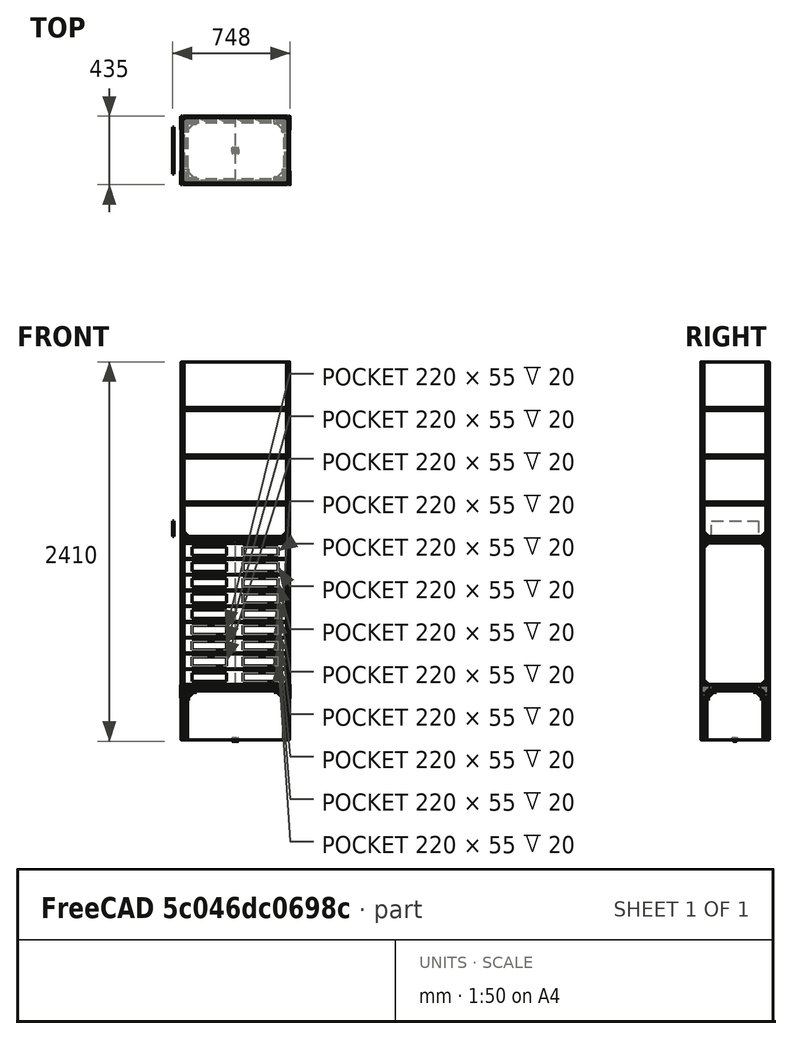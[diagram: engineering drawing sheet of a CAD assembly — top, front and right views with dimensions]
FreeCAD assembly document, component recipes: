
FREECAD ASSEMBLY — COMPONENT RECIPES ("2020 shelf")

This assembly document has 11 components, labeled P0..P10 below (a component is one placed body or linked part). 9 of them carry a construction recipe — the FreeCAD feature program that regenerates the part from scratch, quoted from this document or its linked companion documents; the rest are supplied as boundary geometry only. No exploded tour is included for this assembly.
COMPONENT P0 — recipe-attached ("Cabinet", modeled in this document).
Construction recipe (the document's own serialized feature program — sketch geometry with constraints, then the solid features built on it; lengths are millimeters unless a unit is written):

FEATURE [Sketcher::SketchObject] Sketch016
  ArcFitTolerance = 1e-06
  AttachmentSupport = -> [XY_Plane007]
  FullyConstrained = true
  MakeInternals = false
  MapMode = 5
  sketch-geometry (8):
    g0: LineSegment StartX=20 StartY=0 StartZ=0 EndX=305 EndY=0 EndZ=0
    g1: LineSegment StartX=325 StartY=20 StartZ=0 EndX=325 EndY=435 EndZ=0
    g2: LineSegment StartX=325 StartY=435 StartZ=0 EndX=0 EndY=435 EndZ=0
    g3: LineSegment StartX=0 StartY=435 StartZ=0 EndX=0 EndY=20 EndZ=0
    g4: ArcOfCircle CenterX=20 CenterY=20 CenterZ=0 NormalX=0 NormalY=0 NormalZ=1 AngleXU=0 Radius=20 StartAngle=3.14159 EndAngle=4.71239
    g5: GeomPoint [constr] X=0 Y=0 Z=0
    g6: ArcOfCircle CenterX=305 CenterY=20 CenterZ=0 NormalX=0 NormalY=0 NormalZ=1 AngleXU=0 Radius=20 StartAngle=4.71239 EndAngle=6.28319
    g7: GeomPoint [constr] X=325 Y=0 Z=0
  constraints (19):
    c: Coincident(g1,g2)
    c: Coincident(g2,g3)
    c: Horizontal(g0)
    c: Horizontal(g2)
    c: Vertical(g1)
    c: Vertical(g3)
    c: Coincident(g5,g-1)
    c: DistanceX(g5,g7) = 325
    c: DistanceY(g7,g1) = 435
    c: PointOnObject(g5,g3)
    c: PointOnObject(g5,g0)
    c: Tangent(g3,g4) = -1.5708
    c: Tangent(g0,g4) = -1.5708
    c: PointOnObject(g7,g0)
    c: PointOnObject(g7,g1)
    c: Tangent(g0,g6) = -1.5708
    c: Tangent(g1,g6) = -1.5708
    c: Equal(g4,g6)
    c: Radius(g6) = 20
FEATURE [PartDesign::Pad] Pad009
  Direction = (0,0,1)
  Length = 920
  Length2 = 10
  Profile = -> Sketch016
  ReferenceAxis = -> Sketch016 [N_Axis]
  Suppressed = false
  Type = 0
FEATURE [Sketcher::SketchObject] Sketch017
  ArcFitTolerance = 1e-06
  AttachmentSupport = -> [XZ_Plane007]
  FullyConstrained = true
  MakeInternals = false
  MapMode = 5
  Placement = pos=(0,0,0) rot=(1,0,0;1.5708rad)
  sketch-geometry (9):
    g0: LineSegment StartX=50 StartY=75 StartZ=0 EndX=50 EndY=20 EndZ=0
    g1: LineSegment StartX=50 StartY=20 StartZ=0 EndX=270 EndY=20 EndZ=0
    g2: LineSegment StartX=270 StartY=20 StartZ=0 EndX=270 EndY=75 EndZ=0
    g3: LineSegment StartX=270 StartY=75 StartZ=0 EndX=50 EndY=75 EndZ=0
    g4: GeomPoint [constr] X=160 Y=47.5 Z=0
    g5: LineSegment StartX=0 StartY=100 StartZ=0 EndX=0 EndY=95 EndZ=0
    g6: LineSegment StartX=0 StartY=95 StartZ=0 EndX=320 EndY=95 EndZ=0
    g7: LineSegment StartX=320 StartY=95 StartZ=0 EndX=320 EndY=100 EndZ=0
    g8: LineSegment StartX=320 StartY=100 StartZ=0 EndX=0 EndY=100 EndZ=0
  constraints (26):
    c: Coincident(g0,g1)
    c: Coincident(g1,g2)
    c: Coincident(g2,g3)
    c: Coincident(g3,g0)
    c: Vertical(g0)
    c: Vertical(g2)
    c: Horizontal(g1)
    c: Horizontal(g3)
    c: Symmetric(g2,g0,g4)
    c: Coincident(g5,g6)
    c: Coincident(g6,g7)
    c: Coincident(g7,g8)
    c: Coincident(g8,g5)
    c: Vertical(g5)
    c: Vertical(g7)
    c: Horizontal(g6)
    c: Horizontal(g8)
    c: PointOnObject(g5,g-2)
    c: Distance(g8,g8) = 320
    c: DistanceX(g-1,g4) = 160
    c: DistanceX(g-1,g0) = 50
    c: Distance(g0,g6) = 20
    c: DistanceY(g-1,g0) = 20
    c: DistanceY(g0,g0) = 55
    c: DistanceY(g7,g7) = 5
    c: DistanceY(g-1,g7) = 100
FEATURE [PartDesign::Pocket] Pocket002
  BaseFeature = -> Pad009
  Direction = (0,1,-2e-16)
  Length = 20
  Length2 = 5
  Profile = -> Sketch017
  ReferenceAxis = -> Sketch017 [N_Axis]
  Suppressed = false
  Type = 0
FEATURE [PartDesign::LinearPattern] LinearPattern
  BaseFeature = -> Pocket002
  Direction = -> Z_Axis007
  Length = 800
  Mode = 1
  Occurrences = 9
  Offset = 100
  Originals = -> [Pocket002]
  Suppressed = false
  TransformMode = 0
FEATURE [PartDesign::Body] Body007  label="Cabinet"
  AllowCompound = true
  Group = -> [Sketch016,Pad009,Sketch017,Pocket002,LinearPattern]
  Origin = -> Origin007
  Tip = -> LinearPattern
COMPONENT P1 — recipe-attached ("2040", modeled in this document).
Construction recipe (the document's own serialized feature program — sketch geometry with constraints, then the solid features built on it; lengths are millimeters unless a unit is written):

FEATURE [PartDesign::SubShapeBinder] Binder002
  BindCopyOnChange = 0
  BindMode = 0
  ClaimChildren = false
  Context = -> Body008 [Binder002.]
  Fuse = false
  MakeFace = true
  OffsetFill = false
  OffsetIntersection = false
  OffsetJoinType = 0
  OffsetOpenResult = false
  PartialLoad = false
  Placement = pos=(10,0,0) rot=(0,0,1;0rad)
  Relative = true
  Support = -> [Body001[Binder001.]]
  _Version = 2
FEATURE [PartDesign::Pad] Pad010
  Direction = (0,0,-1)
  Length = 10
  Length2 = 10
  Placement = pos=(10,0,0) rot=(0,0,1;0rad)
  Profile = -> Binder002
  Suppressed = false
  Type = 0
FEATURE [PartDesign::Mirrored] Mirrored003
  BaseFeature = -> Pad010
  MirrorPlane = -> YZ_Plane008
  Placement = pos=(10,0,0) rot=(0,0,1;0rad)
  Refine = true
  Suppressed = false
  TransformMode = 1
FEATURE [Sketcher::SketchObject] Sketch019
  ArcFitTolerance = 1e-06
  AttachmentSupport = -> [XY_Plane008]
  FullyConstrained = true
  MakeInternals = false
  MapMode = 5
  sketch-geometry (5):
    g0: LineSegment StartX=-1.5 StartY=10 StartZ=0 EndX=1.5 EndY=10 EndZ=0
    g1: LineSegment StartX=1.5 StartY=10 StartZ=0 EndX=1.5 EndY=7 EndZ=0
    g2: LineSegment StartX=1.5 StartY=7 StartZ=0 EndX=-1.5 EndY=7 EndZ=0
    g3: LineSegment StartX=-1.5 StartY=7 StartZ=0 EndX=-1.5 EndY=10 EndZ=0
    g4: GeomPoint [constr] X=0 Y=8.5 Z=0
  constraints (13):
    c: Coincident(g0,g1)
    c: Coincident(g1,g2)
    c: Coincident(g2,g3)
    c: Coincident(g3,g0)
    c: Horizontal(g0)
    c: Horizontal(g2)
    c: Vertical(g1)
    c: Vertical(g3)
    c: Symmetric(g2,g0,g4)
    c: PointOnObject(g4,g-2)
    c: Equal(g1,g2)
    c: DistanceX(g2,g2) = 3
    c: DistanceY(g-1,g0) = 10
FEATURE [PartDesign::Pad] Pad011
  BaseFeature = -> Mirrored003
  Direction = (0,0,1)
  Length = 10
  Length2 = 10
  Placement = pos=(10,0,0) rot=(0,0,1;0rad)
  Profile = -> Sketch019
  ReferenceAxis = -> Sketch019 [N_Axis]
  Refine = true
  Reversed = true
  Suppressed = false
  Type = 0
FEATURE [PartDesign::Mirrored] Mirrored004
  BaseFeature = -> Pad011
  MirrorPlane = -> XZ_Plane008
  Originals = -> [Pad011]
  Placement = pos=(10,0,0) rot=(0,0,1;0rad)
  Refine = true
  Suppressed = false
  TransformMode = 0
FEATURE [PartDesign::SubShapeBinder] Binder003  label="2040 Profile"
  BindCopyOnChange = 0
  BindMode = 0
  ClaimChildren = false
  Context = -> Body008 [Binder003.]
  Fuse = false
  MakeFace = true
  OffsetFill = false
  OffsetIntersection = false
  OffsetJoinType = 0
  OffsetOpenResult = false
  PartialLoad = false
  Relative = true
  Support = -> [Mirrored004[Face96]]
  _Version = 2
FEATURE [PartDesign::Body] Body008  label="2040"
  AllowCompound = true
  Group = -> [Binder002,Pad010,Mirrored003,Sketch019,Pad011,Mirrored004,Binder003]
  Origin = -> Origin008
  Tip = -> Mirrored004
COMPONENT P2 — recipe-attached ("4420", modeled in this document).
Construction recipe (the document's own serialized feature program — sketch geometry with constraints, then the solid features built on it; lengths are millimeters unless a unit is written):

FEATURE [PartDesign::SubShapeBinder] Binder004
  BindCopyOnChange = 0
  BindMode = 0
  ClaimChildren = false
  Context = -> Body009 [Binder004.]
  Fuse = false
  MakeFace = true
  OffsetFill = false
  OffsetIntersection = false
  OffsetJoinType = 0
  OffsetOpenResult = false
  PartialLoad = false
  Placement = pos=(0,10,0) rot=(0,0,1;0rad)
  Relative = true
  Support = -> [Body008[Binder003.]]
  _Version = 2
FEATURE [PartDesign::Pad] Pad012
  Direction = (0,0,1)
  Length = 10
  Length2 = 10
  Placement = pos=(0,10,0) rot=(0,0,1;0rad)
  Profile = -> Binder004
  Suppressed = false
  Type = 0
FEATURE [PartDesign::Mirrored] Mirrored005
  BaseFeature = -> Pad012
  MirrorPlane = -> XZ_Plane009
  Placement = pos=(0,10,0) rot=(0,0,1;0rad)
  Refine = true
  Suppressed = false
  TransformMode = 1
FEATURE [Sketcher::SketchObject] Sketch020
  ArcFitTolerance = 1e-06
  AttachmentSupport = -> [XY_Plane009]
  FullyConstrained = true
  MakeInternals = false
  MapMode = 5
  sketch-geometry (5):
    g0: LineSegment StartX=-17 StartY=-1.5 StartZ=0 EndX=-17 EndY=1.5 EndZ=0
    g1: LineSegment StartX=-17 StartY=1.5 StartZ=0 EndX=-20 EndY=1.5 EndZ=0
    g2: LineSegment StartX=-20 StartY=1.5 StartZ=0 EndX=-20 EndY=-1.5 EndZ=0
    g3: LineSegment StartX=-20 StartY=-1.5 StartZ=0 EndX=-17 EndY=-1.5 EndZ=0
    g4: GeomPoint [constr] X=-18.5 Y=0 Z=0
  constraints (13):
    c: Coincident(g0,g1)
    c: Coincident(g1,g2)
    c: Coincident(g2,g3)
    c: Coincident(g3,g0)
    c: Vertical(g0)
    c: Vertical(g2)
    c: Horizontal(g1)
    c: Horizontal(g3)
    c: Symmetric(g2,g0,g4)
    c: PointOnObject(g4,g-1)
    c: Equal(g2,g1)
    c: Distance(g2,g2) = 3
    c: DistanceX(g1,g-1) = 20
FEATURE [PartDesign::Pad] Pad013
  BaseFeature = -> Mirrored005
  Direction = (0,0,1)
  Length = 10
  Length2 = 10
  Placement = pos=(0,10,0) rot=(0,0,1;0rad)
  Profile = -> Sketch020
  ReferenceAxis = -> Sketch020 [N_Axis]
  Refine = true
  Suppressed = false
  Type = 0
FEATURE [PartDesign::Mirrored] Mirrored006
  BaseFeature = -> Pad013
  MirrorPlane = -> Sketch020 [V_Axis]
  Originals = -> [Pad013]
  Placement = pos=(0,10,0) rot=(0,0,1;0rad)
  Refine = true
  Suppressed = false
  TransformMode = 0
FEATURE [PartDesign::SubShapeBinder] Binder005  label="4420 Profile"
  BindCopyOnChange = 0
  BindMode = 0
  ClaimChildren = false
  Context = -> Body009 [Binder005.]
  Fuse = false
  MakeFace = true
  OffsetFill = false
  OffsetIntersection = false
  OffsetJoinType = 0
  OffsetOpenResult = false
  PartialLoad = false
  Relative = true
  Support = -> [Mirrored006[Face124]]
  _Version = 2
FEATURE [PartDesign::Body] Body009  label="4420"
  AllowCompound = true
  Group = -> [Binder004,Pad012,Mirrored005,Sketch020,Pad013,Mirrored006,Binder005]
  Origin = -> Origin009
  Tip = -> Mirrored006
COMPONENT P3 — recipe-attached ("Body010", modeled in this document).
Construction recipe (the document's own serialized feature program — sketch geometry with constraints, then the solid features built on it; lengths are millimeters unless a unit is written):

FEATURE [PartDesign::SubShapeBinder] Binder006
  BindCopyOnChange = 0
  BindMode = 0
  ClaimChildren = false
  Context = -> Body010 [Binder006.]
  Fuse = false
  MakeFace = true
  OffsetFill = false
  OffsetIntersection = false
  OffsetJoinType = 0
  OffsetOpenResult = false
  PartialLoad = false
  Relative = true
  Support = -> [Body[Binder.]]
  _Version = 2
FEATURE [Sketcher::SketchObject] Sketch022
  ArcFitTolerance = 1e-06
  AttachmentSupport = -> [XY_Plane010]
  ExternalGeometry = -> [Binder006]
  FullyConstrained = true
  MakeInternals = false
  MapMode = 5
  sketch-geometry (5):
    g0: LineSegment StartX=-335 StartY=-187.5 StartZ=0 EndX=335 EndY=-187.5 EndZ=0
    g1: LineSegment StartX=335 StartY=-187.5 StartZ=0 EndX=335 EndY=187.5 EndZ=0
    g2: LineSegment StartX=335 StartY=187.5 StartZ=0 EndX=-335 EndY=187.5 EndZ=0
    g3: LineSegment StartX=-335 StartY=187.5 StartZ=0 EndX=-335 EndY=-187.5 EndZ=0
    g4: GeomPoint [constr] X=0 Y=0 Z=0
  constraints (12):
    c: Coincident(g0,g1)
    c: Coincident(g1,g2)
    c: Coincident(g2,g3)
    c: Coincident(g3,g0)
    c: Horizontal(g0)
    c: Horizontal(g2)
    c: Vertical(g1)
    c: Vertical(g3)
    c: Symmetric(g2,g0,g4)
    c: Coincident(g4,g-1)
    c: Vertical(g-3,g1)
    c: Distance(g-3,g1) = 20
FEATURE [PartDesign::Pad] Pad014
  Direction = (0,0,1)
  Length = 310
  Length2 = 10
  Profile = -> Sketch022
  ReferenceAxis = -> Sketch022 [N_Axis]
  Suppressed = false
  Type = 0
  expr: Length = VarSet.StiltHeight - 40 mm
FEATURE [PartDesign::SubShapeBinder] Binder007
  BindCopyOnChange = 0
  BindMode = 0
  ClaimChildren = false
  Context = -> Body010 [Binder007.]
  Fuse = false
  MakeFace = true
  OffsetFill = false
  OffsetIntersection = false
  OffsetJoinType = 0
  OffsetOpenResult = false
  PartialLoad = false
  Relative = true
  Support = -> [Pad014[Edge8,Edge1,Edge2,Edge5]]
  _Version = 2
FEATURE [PartDesign::Body] Body010
  AllowCompound = true
  Group = -> [Binder006,Sketch022,Pad014,Binder007]
  Origin = -> Origin010
  Tip = -> Pad014
COMPONENT P4 — recipe-attached ("TPDD-2040L-", modeled in this document).
Construction recipe (the document's own serialized feature program — sketch geometry with constraints, then the solid features built on it; lengths are millimeters unless a unit is written):

FEATURE [Sketcher::SketchObject] Sketch023
  ArcFitTolerance = 1e-06
  AttachmentSupport = -> [XY_Plane011]
  FullyConstrained = true
  MakeInternals = false
  MapMode = 5
  sketch-geometry (38):
    g0: LineSegment StartX=-9 StartY=75 StartZ=0 EndX=-9 EndY=-8 EndZ=0
    g1: LineSegment StartX=-8 StartY=-9 StartZ=0 EndX=75 EndY=-9 EndZ=0
    g2: LineSegment StartX=76 StartY=-8 StartZ=0 EndX=76 EndY=28 EndZ=0
    g3: LineSegment StartX=75 StartY=29 StartZ=0 EndX=29 EndY=29 EndZ=0
    g4: LineSegment StartX=29 StartY=29 StartZ=0 EndX=29 EndY=75 EndZ=0
    g5: LineSegment StartX=28 StartY=76 StartZ=0 EndX=-8 EndY=76 EndZ=0
    g6: ArcOfCircle CenterX=-8 CenterY=75 CenterZ=0 NormalX=0 NormalY=0 NormalZ=1 AngleXU=0 Radius=1 StartAngle=1.5708 EndAngle=3.14159
    g7: GeomPoint [constr] X=-9 Y=76 Z=0
    g8: ArcOfCircle CenterX=28 CenterY=75 CenterZ=0 NormalX=0 NormalY=0 NormalZ=1 AngleXU=0 Radius=1 StartAngle=1.8e-15 EndAngle=1.5708
    g9: GeomPoint [constr] X=29 Y=76 Z=0
    g10: ArcOfCircle CenterX=75 CenterY=28 CenterZ=0 NormalX=0 NormalY=0 NormalZ=1 AngleXU=0 Radius=1 StartAngle=1.941e-13 EndAngle=1.5708
    g11: GeomPoint [constr] X=76 Y=29 Z=0
    g12: ArcOfCircle CenterX=75 CenterY=-8 CenterZ=0 NormalX=0 NormalY=0 NormalZ=1 AngleXU=0 Radius=1 StartAngle=4.71239 EndAngle=6.28319
    g13: GeomPoint [constr] X=76 Y=-9 Z=0
    g14: ArcOfCircle CenterX=-8 CenterY=-8 CenterZ=0 NormalX=0 NormalY=0 NormalZ=1 AngleXU=0 Radius=1 StartAngle=3.14159 EndAngle=4.71239
    g15: GeomPoint [constr] X=-9 Y=-9 Z=0
    g16: LineSegment [constr] StartX=0 StartY=66 StartZ=0 EndX=0 EndY=46 EndZ=0
    g17: LineSegment [constr] StartX=0 StartY=46 StartZ=0 EndX=20 EndY=46 EndZ=0
    g18: LineSegment [constr] StartX=20 StartY=46 StartZ=0 EndX=20 EndY=66 EndZ=0
    g19: LineSegment [constr] StartX=20 StartY=66 StartZ=0 EndX=0 EndY=66 EndZ=0
    g20: GeomPoint [constr] X=10 Y=56 Z=0
    g21: LineSegment [constr] StartX=46 StartY=20 StartZ=0 EndX=46 EndY=0 EndZ=0
    g22: LineSegment [constr] StartX=46 StartY=0 StartZ=0 EndX=66 EndY=0 EndZ=0
    g23: LineSegment [constr] StartX=66 StartY=0 StartZ=0 EndX=66 EndY=20 EndZ=0
    g24: LineSegment [constr] StartX=66 StartY=20 StartZ=0 EndX=46 EndY=20 EndZ=0
    g25: GeomPoint [constr] X=56 Y=10 Z=0
    g26: GeomPoint [constr] X=10 Y=76 Z=0
    g27: GeomPoint [constr] X=76 Y=10 Z=0
    g28: LineSegment [constr] StartX=10 StartY=76 StartZ=0 EndX=10 EndY=10 EndZ=0
    g29: LineSegment [constr] StartX=10 StartY=10 StartZ=0 EndX=76 EndY=10 EndZ=0
    g30: Circle CenterX=0 CenterY=66 CenterZ=0 NormalX=0 NormalY=0 NormalZ=1 AngleXU=0 Radius=2.75
    g31: Circle CenterX=20 CenterY=66 CenterZ=0 NormalX=0 NormalY=0 NormalZ=1 AngleXU=0 Radius=2.75
    g32: Circle CenterX=0 CenterY=46 CenterZ=0 NormalX=0 NormalY=0 NormalZ=1 AngleXU=0 Radius=2.75
    g33: Circle CenterX=20 CenterY=46 CenterZ=0 NormalX=0 NormalY=0 NormalZ=1 AngleXU=0 Radius=2.75
    g34: Circle CenterX=46 CenterY=20 CenterZ=0 NormalX=0 NormalY=0 NormalZ=1 AngleXU=0 Radius=2.75
    g35: Circle CenterX=66 CenterY=20 CenterZ=0 NormalX=0 NormalY=0 NormalZ=1 AngleXU=0 Radius=2.75
    g36: Circle CenterX=46 CenterY=0 CenterZ=0 NormalX=0 NormalY=0 NormalZ=1 AngleXU=0 Radius=2.75
    g37: Circle CenterX=66 CenterY=0 CenterZ=0 NormalX=0 NormalY=0 NormalZ=1 AngleXU=0 Radius=2.75
  constraints (87):
    c: Vertical(g0)
    c: Horizontal(g1)
    c: Vertical(g2)
    c: Coincident(g3,g4)
    c: Vertical(g4)
    c: Horizontal(g5)
    c: Horizontal(g3)
    c: DistanceX(g15,g13) = 85
    c: DistanceY(g13,g11) = 38
    c: PointOnObject(g7,g5)
    c: PointOnObject(g7,g0)
    c: Tangent(g5,g6) = -1.5708
    c: Tangent(g0,g6) = -1.5708
    c: PointOnObject(g9,g5)
    c: PointOnObject(g9,g4)
    c: Tangent(g5,g8) = -1.5708
    c: Tangent(g4,g8) = -1.5708
    c: PointOnObject(g11,g3)
    c: PointOnObject(g11,g2)
    c: Tangent(g3,g10) = -1.5708
    c: Tangent(g2,g10) = -1.5708
    c: PointOnObject(g13,g2)
    c: PointOnObject(g13,g1)
    c: Tangent(g2,g12) = -1.5708
    c: Tangent(g1,g12) = -1.5708
    c: PointOnObject(g15,g0)
    c: PointOnObject(g15,g1)
    c: Tangent(g0,g14) = -1.5708
    c: Tangent(g1,g14) = -1.5708
    c: Equal(g6,g8)
    c: Equal(g8,g10)
    c: Equal(g10,g12)
    c: Equal(g12,g14)
    c: Radius(g6) = 1
    c: Equal(g0,g1)
    c: Equal(g5,g2)
    c: Coincident(g16,g17)
    c: Coincident(g17,g18)
    c: Coincident(g18,g19)
    c: Coincident(g19,g16)
    c: Vertical(g16)
    c: Vertical(g18)
    c: Horizontal(g17)
    c: Horizontal(g19)
    c: Symmetric(g18,g16,g20)
    c: Coincident(g21,g22)
    c: Coincident(g22,g23)
    c: Coincident(g23,g24)
    c: Coincident(g24,g21)
    c: Vertical(g21)
    c: Vertical(g23)
    c: Horizontal(g22)
    c: Horizontal(g24)
    c: Symmetric(g23,g21,g25)
    c: Symmetric(g5,g5,g26)
    c: Symmetric(g2,g2,g27)
    c: Coincident(g28,g26)
    c: Vertical(g28)
    c: Coincident(g29,g28)
    c: Coincident(g29,g27)
    c: Horizontal(g29)
    c: Equal(g22,g23)
    c: Equal(g17,g18)
    c: Equal(g17,g24)
    c: PointOnObject(g25,g29)
    c: PointOnObject(g20,g28)
    c: Distance(g19,g19) = 20
    c: Distance(g16,g1) = 55
    c: Distance(g21,g0) = 55
    c: Coincident(g30,g16)
    c: Coincident(g31,g18)
    c: Coincident(g32,g16)
    c: Coincident(g33,g17)
    c: Coincident(g34,g21)
    c: Coincident(g35,g23)
    c: Coincident(g36,g21)
    c: Coincident(g37,g22)
    c: Equal(g30,g31)
    c: Equal(g31,g32)
    c: Equal(g32,g33)
    c: Equal(g33,g34)
    c: Equal(g34,g35)
    c: Equal(g35,g36)
    c: Equal(g36,g37)
    c: Diameter(g31) = 5.5
    c: PointOnObject(g16,g-2)
    c: PointOnObject(g21,g-1)
FEATURE [PartDesign::Pad] Pad015
  Direction = (0,0,1)
  Length = 3
  Length2 = 10
  Profile = -> Sketch023
  ReferenceAxis = -> Sketch023 [N_Axis]
  Suppressed = false
  Type = 0
FEATURE [PartDesign::Body] Body011  label="TPDD-2040L-"
  AllowCompound = true
  Group = -> [Sketch023,Pad015]
  Origin = -> Origin011
  Tip = -> Pad015
COMPONENT P5 — recipe-attached ("Panels", modeled in this document).
Construction recipe (the document's own serialized feature program — sketch geometry with constraints, then the solid features built on it; lengths are millimeters unless a unit is written):

FEATURE [Sketcher::SketchObject] Sketch024
  ArcFitTolerance = 1e-06
  AttachmentOffset = pos=(0,0,-400) rot=(0,0,1;0rad)
  AttachmentSupport = -> [YZ_Plane012]
  FullyConstrained = true
  MakeInternals = false
  MapMode = 5
  Placement = pos=(-400,0,0) rot=(0.57735,0.57735,0.57735;2.0944rad)
  sketch-geometry (5):
    g0: LineSegment StartX=150 StartY=1290 StartZ=0 EndX=-150 EndY=1290 EndZ=0
    g1: LineSegment StartX=-150 StartY=1290 StartZ=0 EndX=-150 EndY=1390 EndZ=0
    g2: LineSegment StartX=-150 StartY=1390 StartZ=0 EndX=150 EndY=1390 EndZ=0
    g3: LineSegment StartX=150 StartY=1390 StartZ=0 EndX=150 EndY=1290 EndZ=0
    g4: GeomPoint [constr] X=1e-16 Y=1340 Z=0
  constraints (13):
    c: Coincident(g0,g1)
    c: Coincident(g1,g2)
    c: Coincident(g2,g3)
    c: Coincident(g3,g0)
    c: Horizontal(g0)
    c: Horizontal(g2)
    c: Vertical(g1)
    c: Vertical(g3)
    c: Symmetric(g2,g0,g4)
    c: PointOnObject(g4,g-2)
    c: Distance(g1,g1) = 100
    c: Distance(g2,g2) = 300
    c: DistanceY(g-1,g0) = 1290
FEATURE [PartDesign::Pad] Pad016
  Direction = (1,0,0)
  Length = 10
  Length2 = 10
  Placement = pos=(0,0,0) rot=(1,1,1;2.0944rad)
  Profile = -> Sketch024
  ReferenceAxis = -> Sketch024 [N_Axis]
  Suppressed = false
  Type = 0
FEATURE [PartDesign::Body] Body012  label="Panels"
  AllowCompound = true
  Group = -> [Sketch024,Pad016]
  Origin = -> Origin012
  Tip = -> Pad016
COMPONENT P6 — recipe-attached ("Body013", modeled in this document).
Construction recipe (the document's own serialized feature program — sketch geometry with constraints, then the solid features built on it; lengths are millimeters unless a unit is written):

FEATURE [PartDesign::SubShapeBinder] Binder014  label="Binder021"
  BindCopyOnChange = 0
  BindMode = 0
  ClaimChildren = false
  Context = -> Body013 [Binder014.]
  Fuse = false
  MakeFace = true
  OffsetFill = false
  OffsetIntersection = false
  OffsetJoinType = 0
  OffsetOpenResult = false
  PartialLoad = false
  Relative = true
  Support = -> [Body[Binder.]]
  _Version = 2
FEATURE [Sketcher::SketchObject] Sketch028
  ArcFitTolerance = 1e-06
  AttachmentSupport = -> [XY_Plane013]
  ExternalGeometry = -> [Binder014]
  FullyConstrained = true
  MakeInternals = false
  MapMode = 5
  sketch-geometry (5):
    g0: LineSegment StartX=315 StartY=-197.5 StartZ=0 EndX=315 EndY=197.5 EndZ=0
    g1: LineSegment StartX=315 StartY=197.5 StartZ=0 EndX=-315 EndY=197.5 EndZ=0
    g2: LineSegment StartX=-315 StartY=197.5 StartZ=0 EndX=-315 EndY=-197.5 EndZ=0
    g3: LineSegment StartX=-315 StartY=-197.5 StartZ=0 EndX=315 EndY=-197.5 EndZ=0
    g4: GeomPoint [constr] X=0 Y=0 Z=0
  constraints (12):
    c: Coincident(g0,g1)
    c: Coincident(g1,g2)
    c: Coincident(g2,g3)
    c: Coincident(g3,g0)
    c: Vertical(g0)
    c: Vertical(g2)
    c: Horizontal(g1)
    c: Horizontal(g3)
    c: Symmetric(g2,g0,g4)
    c: Coincident(g4,g-1)
    c: DistanceX(g-3,g1) = 20
    c: DistanceY(g1,g-3) = 10
FEATURE [PartDesign::Pad] Pad017
  Direction = (0,0,1)
  Length = 310
  Length2 = 10
  Profile = -> Sketch028
  ReferenceAxis = -> Sketch028 [N_Axis]
  Suppressed = false
  Type = 0
FEATURE [PartDesign::SubShapeBinder] Binder015  label="Binder022"
  BindCopyOnChange = 0
  BindMode = 0
  ClaimChildren = false
  Context = -> Body013 [Binder015.]
  Fuse = false
  MakeFace = true
  OffsetFill = false
  OffsetIntersection = false
  OffsetJoinType = 0
  OffsetOpenResult = false
  PartialLoad = false
  Relative = true
  Support = -> [Pad017[Edge2,Edge5,Edge8,Edge1]]
  _Version = 2
FEATURE [PartDesign::Body] Body013
  AllowCompound = true
  Group = -> [Sketch028,Binder014,Pad017,Binder015]
  Origin = -> Origin013
  Tip = -> Pad017
COMPONENT P7 — recipe-attached ("TPDC-6034-", modeled in this document).
Construction recipe (the document's own serialized feature program — sketch geometry with constraints, then the solid features built on it; lengths are millimeters unless a unit is written):

FEATURE [Sketcher::SketchObject] Sketch  label="cabinet projection"
  ArcFitTolerance = 1e-06
  AttachmentSupport = -> [XY_Plane]
  FullyConstrained = true
  MakeInternals = false
  MapMode = 5
  sketch-geometry (5):
    g0: LineSegment StartX=-325 StartY=217.5 StartZ=0 EndX=-325 EndY=-217.5 EndZ=0
    g1: LineSegment StartX=-325 StartY=-217.5 StartZ=0 EndX=325 EndY=-217.5 EndZ=0
    g2: LineSegment StartX=325 StartY=-217.5 StartZ=0 EndX=325 EndY=217.5 EndZ=0
    g3: LineSegment StartX=325 StartY=217.5 StartZ=0 EndX=-325 EndY=217.5 EndZ=0
    g4: GeomPoint [constr] X=0 Y=0 Z=0
  constraints (12):
    c: Coincident(g0,g1)
    c: Coincident(g1,g2)
    c: Coincident(g2,g3)
    c: Coincident(g3,g0)
    c: Vertical(g0)
    c: Vertical(g2)
    c: Horizontal(g1)
    c: Horizontal(g3)
    c: Symmetric(g2,g0,g4)
    c: Coincident(g4,g-1)
    c: DistanceX(g1,g1) = 650
    c: DistanceY(g2,g2) = 435
FEATURE [Sketcher::SketchObject] Sketch001
  ArcFitTolerance = 1e-06
  AttachmentSupport = -> [XY_Plane]
  ExternalGeometry = -> [Sketch]
  FullyConstrained = true
  MakeInternals = false
  MapMode = 5
  sketch-geometry (5):
    g0: LineSegment StartX=335 StartY=207.5 StartZ=0 EndX=-335 EndY=207.5 EndZ=0
    g1: LineSegment StartX=-335 StartY=207.5 StartZ=0 EndX=-335 EndY=-207.5 EndZ=0
    g2: LineSegment StartX=-335 StartY=-207.5 StartZ=0 EndX=335 EndY=-207.5 EndZ=0
    g3: LineSegment StartX=335 StartY=-207.5 StartZ=0 EndX=335 EndY=207.5 EndZ=0
    g4: GeomPoint [constr] X=0 Y=0 Z=0
  constraints (12):
    c: Coincident(g0,g1)
    c: Coincident(g1,g2)
    c: Coincident(g2,g3)
    c: Coincident(g3,g0)
    c: Horizontal(g0)
    c: Horizontal(g2)
    c: Vertical(g1)
    c: Vertical(g3)
    c: Symmetric(g2,g0,g4)
    c: Coincident(g4,g-1)
    c: DistanceY(g-6,g1) = 10
    c: DistanceX(g1,g-6) = 10
FEATURE [PartDesign::Pad] Pad
  Direction = (0,0,1)
  Length = 2400
  Length2 = 10
  Profile = -> Sketch001
  ReferenceAxis = -> Sketch001 [N_Axis]
  Suppressed = false
  Type = 0
FEATURE [PartDesign::SubShapeBinder] Binder
  BindCopyOnChange = 0
  BindMode = 0
  ClaimChildren = false
  Context = -> Body [Binder.]
  Fuse = false
  MakeFace = true
  OffsetFill = false
  OffsetIntersection = false
  OffsetJoinType = 0
  OffsetOpenResult = false
  PartialLoad = false
  Relative = true
  Support = -> [Pad[Edge2,Edge5,Edge8,Edge1]]
  _Version = 2
FEATURE [Sketcher::SketchObject] Sketch018
  ArcFitTolerance = 1e-06
  AttachmentOffset = pos=(0,0,330) rot=(0,0,1;0rad)
  AttachmentSupport = -> [XY_Plane]
  ExternalGeometry = -> [Binder]
  FullyConstrained = true
  MakeInternals = false
  MapMode = 5
  Placement = pos=(0,0,330) rot=(0,0,1;0rad)
  expr: .AttachmentOffset.Base.z = VarSet.StiltHeight - 20 mm
  sketch-geometry (6):
    g0: LineSegment StartX=-325 StartY=207.5 StartZ=0 EndX=325 EndY=207.5 EndZ=0
    g1: LineSegment StartX=-325 StartY=-207.5 StartZ=0 EndX=325 EndY=-207.5 EndZ=0
    g2: LineSegment StartX=-325 StartY=197.5 StartZ=0 EndX=-325 EndY=-197.5 EndZ=0
    g3: LineSegment StartX=325 StartY=197.5 StartZ=0 EndX=325 EndY=-197.5 EndZ=0
    g4: LineSegment StartX=-305 StartY=187.5 StartZ=0 EndX=305 EndY=187.5 EndZ=0
    g5: LineSegment StartX=-305 StartY=-187.5 StartZ=0 EndX=305 EndY=-187.5 EndZ=0
  constraints (24):
    c: Horizontal(g0)
    c: Horizontal(g1)
    c: Vertical(g0,g1)
    c: Equal(g0,g1)
    c: DistanceX(g-3,g0) = 10
    c: DistanceX(g0,g-4) = 10
    c: Vertical(g2)
    c: Vertical(g3)
    c: Equal(g2,g3)
    c: Horizontal(g2,g3)
    c: Vertical(g0,g2)
    c: Vertical(g0,g3)
    c: Distance(g0,g2) = 10
    c: Distance(g2,g1) = 10
    c: Horizontal(g1,g-6)
    c: Horizontal(g0,g-3)
    c: Horizontal(g4)
    c: Horizontal(g5)
    c: Vertical(g4,g5)
    c: Equal(g4,g5)
    c: Distance(g4,g0) = 20
    c: DistanceX(g0,g4) = 20
    c: DistanceX(g4,g0) = 20
    c: Distance(g5,g1) = 20
FEATURE [PartDesign::SubShapeBinder] Binder008  label="Binder009"
  BindCopyOnChange = 0
  BindMode = 0
  ClaimChildren = false
  Context = -> Body [Binder008.]
  Fuse = false
  MakeFace = true
  OffsetFill = false
  OffsetIntersection = false
  OffsetJoinType = 0
  OffsetOpenResult = false
  PartialLoad = false
  Relative = true
  Support = -> [Sketch018[Edge1,Edge2]]
  _Version = 2
FEATURE [PartDesign::SubShapeBinder] Binder009  label="Binder011"
  BindCopyOnChange = 0
  BindMode = 0
  ClaimChildren = false
  Context = -> Body [Binder009.]
  Fuse = false
  MakeFace = true
  OffsetFill = false
  OffsetIntersection = false
  OffsetJoinType = 0
  OffsetOpenResult = false
  PartialLoad = false
  Relative = true
  Support = -> [Sketch018[Edge3,Edge4]]
  _Version = 2
FEATURE [PartDesign::SubShapeBinder] Binder010  label="Binder013"
  BindCopyOnChange = 0
  BindMode = 0
  ClaimChildren = false
  Context = -> Body [Binder010.]
  Fuse = false
  MakeFace = true
  OffsetFill = false
  OffsetIntersection = false
  OffsetJoinType = 0
  OffsetOpenResult = false
  PartialLoad = false
  Relative = true
  Support = -> [Sketch018[Edge5,Edge6]]
  _Version = 2
FEATURE [Sketcher::SketchObject] Sketch025
  ArcFitTolerance = 1e-06
  AttachmentOffset = pos=(0,0,1270) rot=(0,0,1;0rad)
  AttachmentSupport = -> [XY_Plane]
  ExternalGeometry = -> [Binder]
  FullyConstrained = true
  MakeInternals = false
  MapMode = 5
  Placement = pos=(0,0,1270) rot=(0,0,1;0rad)
  sketch-geometry (2):
    g0: LineSegment StartX=-335 StartY=197.5 StartZ=0 EndX=-335 EndY=-197.5 EndZ=0
    g1: LineSegment StartX=335 StartY=197.5 StartZ=0 EndX=335 EndY=-197.5 EndZ=0
  constraints (8):
    c: Vertical(g0)
    c: Vertical(g1)
    c: Horizontal(g0,g1)
    c: Equal(g0,g1)
    c: Vertical(g-3,g0)
    c: Vertical(g-4,g1)
    c: Distance(g-3,g0) = 10
    c: Distance(g0,g-5) = 10
FEATURE [Sketcher::SketchObject] Sketch026
  ArcFitTolerance = 1e-06
  AttachmentOffset = pos=(0,0,1280) rot=(0,0,1;0rad)
  AttachmentSupport = -> [XY_Plane]
  ExternalGeometry = -> [Binder]
  FullyConstrained = true
  MakeInternals = false
  MapMode = 5
  Placement = pos=(0,0,1280) rot=(0,0,1;0rad)
  sketch-geometry (2):
    g0: LineSegment StartX=-325 StartY=207.5 StartZ=0 EndX=325 EndY=207.5 EndZ=0
    g1: LineSegment StartX=-325 StartY=-207.5 StartZ=0 EndX=325 EndY=-207.5 EndZ=0
  constraints (8):
    c: Horizontal(g0)
    c: Horizontal(g1)
    c: Horizontal(g0,g-3)
    c: Horizontal(g-5,g1)
    c: Equal(g0,g1)
    c: Vertical(g0,g1)
    c: Distance(g0,g-3) = 10
    c: Distance(g0,g-4) = 10
FEATURE [PartDesign::SubShapeBinder] Binder011  label="Binder015"
  BindCopyOnChange = 0
  BindMode = 0
  ClaimChildren = false
  Context = -> Body [Binder011.]
  Fuse = false
  MakeFace = true
  OffsetFill = false
  OffsetIntersection = false
  OffsetJoinType = 0
  OffsetOpenResult = false
  PartialLoad = false
  Relative = true
  Support = -> [Sketch025]
  _Version = 2
FEATURE [PartDesign::SubShapeBinder] Binder012  label="Binder016"
  BindCopyOnChange = 0
  BindMode = 0
  ClaimChildren = false
  Context = -> Body [Binder012.]
  Fuse = false
  MakeFace = true
  OffsetFill = false
  OffsetIntersection = false
  OffsetJoinType = 0
  OffsetOpenResult = false
  PartialLoad = false
  Relative = true
  Support = -> [Sketch026]
  _Version = 2
FEATURE [Sketcher::SketchObject] Sketch027
  ArcFitTolerance = 1e-06
  AttachmentOffset = pos=(0,0,1500) rot=(0,0,1;0rad)
  AttachmentSupport = -> [XY_Plane]
  ExternalGeometry = -> [Binder]
  FullyConstrained = true
  MakeInternals = false
  MapMode = 5
  Placement = pos=(0,0,1500) rot=(0,0,1;0rad)
  sketch-geometry (4):
    g0: LineSegment StartX=-325 StartY=207.5 StartZ=0 EndX=325 EndY=207.5 EndZ=0
    g1: LineSegment StartX=-335 StartY=197.5 StartZ=0 EndX=-335 EndY=-197.5 EndZ=0
    g2: LineSegment StartX=335 StartY=197.5 StartZ=0 EndX=335 EndY=-197.5 EndZ=0
    g3: LineSegment StartX=-325 StartY=-207.5 StartZ=0 EndX=325 EndY=-207.5 EndZ=0
  constraints (16):
    c: Horizontal(g0)
    c: Vertical(g1)
    c: Vertical(g2)
    c: Horizontal(g3)
    c: Equal(g0,g3)
    c: Equal(g1,g2)
    c: Vertical(g-3,g1)
    c: Vertical(g0,g3)
    c: Vertical(g-4,g2)
    c: Horizontal(g0,g-3)
    c: Horizontal(g1,g2)
    c: Horizontal(g-5,g3)
    c: Distance(g-3,g1) = 10
    c: Distance(g1,g-5) = 10
    c: DistanceX(g-3,g0) = 10
    c: DistanceX(g0,g-4) = 10
FEATURE [PartDesign::SubShapeBinder] Binder013  label="Binder019"
  BindCopyOnChange = 0
  BindMode = 0
  ClaimChildren = false
  Context = -> Body [Binder013.]
  Fuse = false
  MakeFace = true
  OffsetFill = false
  OffsetIntersection = false
  OffsetJoinType = 0
  OffsetOpenResult = false
  PartialLoad = false
  Relative = true
  Support = -> [Sketch027]
  _Version = 2
FEATURE [PartDesign::Body] Body
  AllowCompound = true
  Group = -> [Sketch,Sketch001,Pad,Binder,Sketch018,Binder008,Binder009,Binder010,Sketch025,Sketch026,Binder011,Binder012,Sketch027,Binder013]
  Origin = -> Origin
  Tip = -> Pad
COMPONENT P8 — recipe-attached ("TPDB-2020-", modeled in this document).
Construction recipe (the document's own serialized feature program — sketch geometry with constraints, then the solid features built on it; lengths are millimeters unless a unit is written):

FEATURE [Sketcher::SketchObject] Sketch002
  ArcFitTolerance = 1e-06
  AttachmentSupport = -> [XY_Plane001]
  FullyConstrained = true
  MakeInternals = false
  MapMode = 5
  sketch-geometry (14):
    g0: LineSegment StartX=0 StartY=3.9 StartZ=0 EndX=2.83934 EndY=3.9 EndZ=0
    g1: LineSegment StartX=2.83934 StartY=3.9 StartZ=0 EndX=5.5 EndY=6.56066 EndZ=0
    g2: LineSegment StartX=5.5 StartY=6.56066 StartZ=0 EndX=5.5 EndY=8 EndZ=0
    g3: LineSegment StartX=5.5 StartY=8 StartZ=0 EndX=3.1 EndY=8 EndZ=0
    g4: LineSegment StartX=3.1 StartY=8 StartZ=0 EndX=3.1 EndY=9.5 EndZ=0
    g5: LineSegment StartX=3.1 StartY=9.5 StartZ=0 EndX=3.6 EndY=9.5 EndZ=0
    g6: LineSegment StartX=3.6 StartY=9.5 StartZ=0 EndX=3.6 EndY=10 EndZ=0
    g7: LineSegment StartX=3.6 StartY=10 StartZ=0 EndX=8.50001 EndY=10 EndZ=0
    g8: LineSegment StartX=0 StartY=0 StartZ=0 EndX=0 EndY=3.9 EndZ=0
    g9: LineSegment [constr] StartX=10 StartY=8.50001 StartZ=0 EndX=10 EndY=0 EndZ=0
    g10: ArcOfCircle [constr] CenterX=8.50001 CenterY=8.50001 CenterZ=0 NormalX=0 NormalY=0 NormalZ=1 AngleXU=0 Radius=1.49999 StartAngle=0 EndAngle=1.5708
    g11: GeomPoint [constr] X=10 Y=10 Z=0
    g12: LineSegment StartX=0 StartY=0 StartZ=0 EndX=9.56066 EndY=9.56066 EndZ=0
    g13: ArcOfCircle CenterX=8.50001 CenterY=8.5 CenterZ=0 NormalX=0 NormalY=0 NormalZ=1 AngleXU=0 Radius=1.5 StartAngle=0.785402 EndAngle=1.57079
  constraints (41):
    c: PointOnObject(g0,g-2)
    c: Horizontal(g0)
    c: Coincident(g0,g1)
    c: Coincident(g1,g2)
    c: Vertical(g2)
    c: Coincident(g2,g3)
    c: Horizontal(g3)
    c: Coincident(g3,g4)
    c: Vertical(g4)
    c: Coincident(g4,g5)
    c: Coincident(g5,g6)
    c: Coincident(g6,g7)
    c: Horizontal(g7)
    c: Coincident(g8,g0)
    c: Vertical(g6)
    c: Horizontal(g5)
    c: Distance(g8,g8) = 3.9
    c: DistanceX(g-1,g11) = 10
    c: DistanceY(g-1,g11) = 10
    c: Distance(g3,g0) = 4.1
    c: Equal(g5,g6)
    c: Distance(g6,g6) = 0.5
    c: DistanceY(g3,g6) = 2
    c: PointOnObject(g9,g-1)
    c: Vertical(g9)
    c: PointOnObject(g11,g7)
    c: PointOnObject(g11,g9)
    c: Tangent(g7,g10) = 1.5708
    c: Tangent(g9,g10) = 1.5708
    c: Coincident(g12,g8)
    c: PointOnObject(g12,g10)
    c: PointOnObject(g10,g12)
    c: Coincident(g13,g7)
    c: Coincident(g13,g12)
    c: Tangent(g13,g10)
    c: Coincident(g8,g-1)
    c: Parallel(g1,g12)
    c: Distance(g0,g12) = 0.75
    c: DistanceX(g-1,g2) = 5.5
    c: DistanceX(g-1,g3) = 3.1
    c: Radius(g13) = 1.5
FEATURE [PartDesign::Pad] Pad001
  Direction = (0,0,1)
  Length = 1
  Length2 = 10
  Profile = -> Sketch002
  ReferenceAxis = -> Sketch002 [N_Axis]
  Suppressed = false
  Type = 0
FEATURE [PartDesign::Plane] DatumPlane
  AttachmentOffset = pos=(0,0,0) rot=(0.862856,0.357407,0.357407;1.71777rad)
  AttachmentSupport = -> [XY_Plane001]
  Length = 82.6027
  MapMode = 5
  Placement = pos=(0,0,0) rot=(0.862856,0.357407,0.357407;1.71777rad)
  ResizeMode = 0
  Width = 61.8921
FEATURE [PartDesign::Mirrored] Mirrored
  MirrorPlane = -> DatumPlane
  Suppressed = false
  TransformMode = 0
FEATURE [PartDesign::Mirrored] Mirrored001
  MirrorPlane = -> YZ_Plane001
  Suppressed = false
  TransformMode = 0
FEATURE [PartDesign::Mirrored] Mirrored002
  MirrorPlane = -> XZ_Plane001
  Suppressed = false
  TransformMode = 0
FEATURE [PartDesign::MultiTransform] MultiTransform
  BaseFeature = -> Pad001
  Refine = true
  Suppressed = false
  TransformMode = 1
  Transformations = -> [Mirrored,Mirrored001,Mirrored002]
FEATURE [PartDesign::SubShapeBinder] Binder001  label="2020 Profile"
  BindCopyOnChange = 0
  BindMode = 0
  ClaimChildren = false
  Context = -> Body001 [Binder001.]
  Fuse = false
  MakeFace = true
  OffsetFill = false
  OffsetIntersection = false
  OffsetJoinType = 0
  OffsetOpenResult = false
  PartialLoad = false
  Relative = true
  Support = -> [MultiTransform[Face34]]
  _Version = 2
FEATURE [PartDesign::Body] Body001  label="2020"
  AllowCompound = true
  Group = -> [Sketch002,Pad001,DatumPlane,MultiTransform,Mirrored,Mirrored001,Mirrored002,Binder001]
  Origin = -> Origin001
  Tip = -> MultiTransform
COMPONENT P9 — geometry summary ("TPDD-2020T-"; no construction recipe available for this part):
  bounding box: 65.0 x 60.0 x 3.0 mm
  tessellated surface: 540 triangles
  volume: 5493 mm^3 (47% of its bounding box)
  symmetry: 2-fold rotationally symmetric about the x axis; mirror-symmetric across its y mid-plane, z mid-plane
COMPONENT P10 — geometry summary ("TPDG-D5-"; no construction recipe available for this part):
  bounding box: 25.5 x 24.5 x 9.1 mm
  tessellated surface: 84 triangles
  volume: 1571 mm^3 (28% of its bounding box)
  symmetry: mirror-symmetric across its z mid-plane
PROVENANCE & LICENSES
A FreeCAD (.FCStd) document from a public repository crawl; recipes are the document's own serialized feature recipes (and, for linked parts, companion documents' recipes).
License: as declared in the source repository (recorded in the dataset sidecar).
